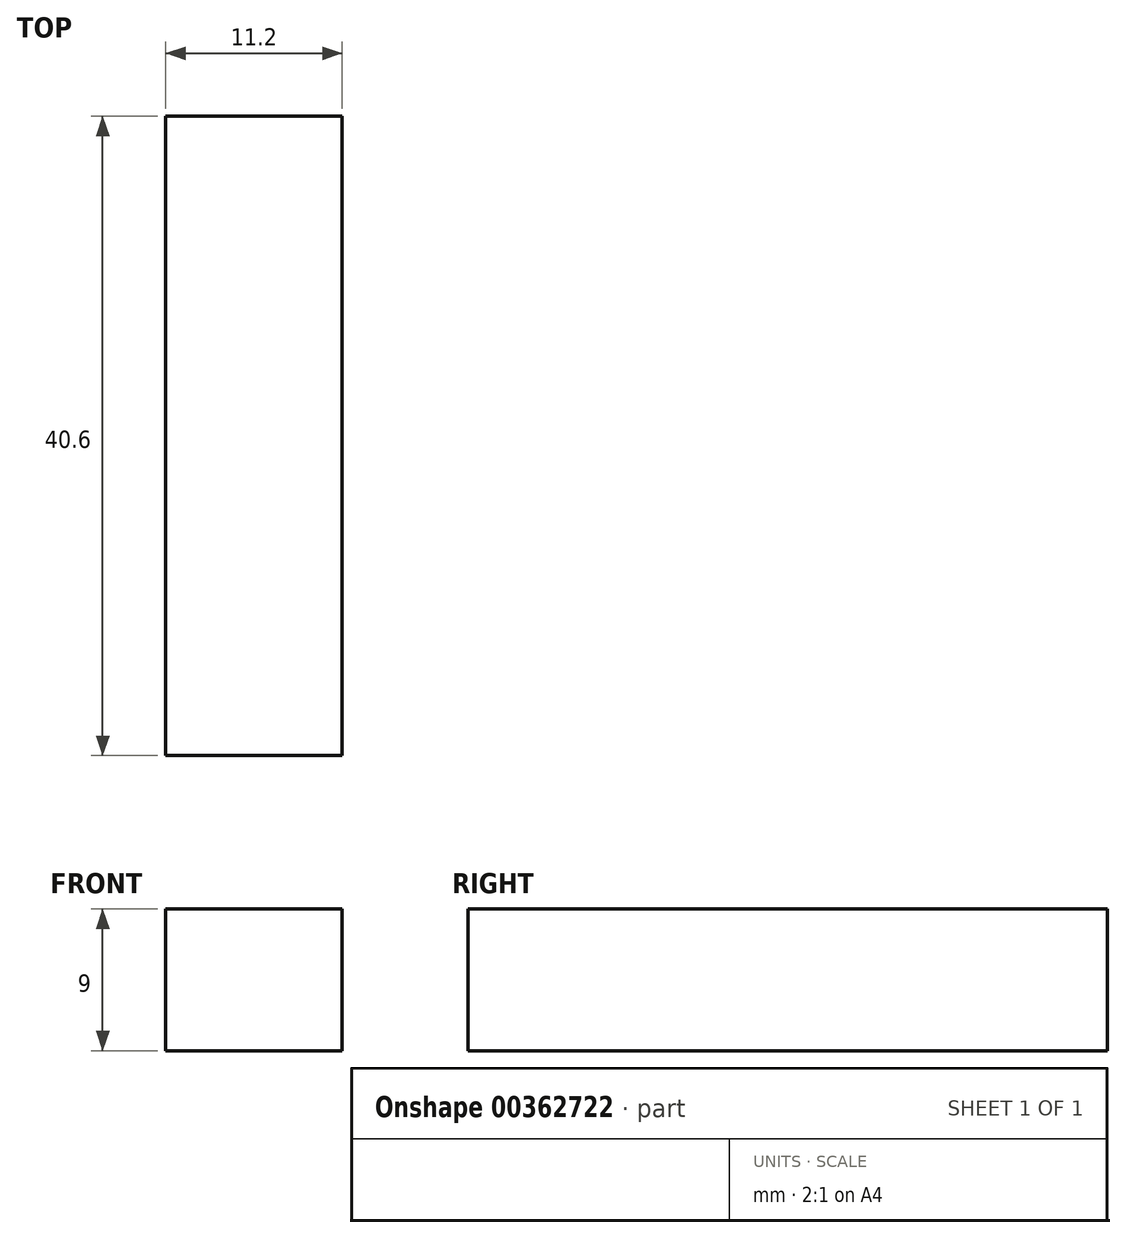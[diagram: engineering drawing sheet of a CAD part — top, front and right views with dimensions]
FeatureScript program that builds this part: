
annotation { "Feature Type Name" : "Feature", "Feature Type Description" : "" }
export const myFeature = defineFeature(function(context is Context, id is Id, definition is map)
    precondition{}
    {
        {
            var Q0;
            Q0=qCreatedBy(makeId("Front.planeOp"),FACE);
            var sketch = newSketch(context, id + "F0", { "sketchPlane" : qUnion([Q0])});
            skLineSegment(sketch, "E0.bottom", {"start": v(5.6, -4.5) * mm, "end": v(-5.6, -4.5) * mm});
            skLineSegment(sketch, "E0.top", {"start": v(5.6, 4.5) * mm, "end": v(-5.6, 4.5) * mm});
            skLineSegment(sketch, "E0.left", {"start": v(5.6, -4.5) * mm, "end": v(5.6, 4.5) * mm});
            skLineSegment(sketch, "E0.right", {"start": v(-5.6, -4.5) * mm, "end": v(-5.6, 4.5) * mm});
            skPoint(sketch, "E0.middle", {"position": v(0, 0) * mm});
            skSolve(sketch);
        }
        {
            var Q0;
            Q0=makeQuery(id+"F0.imprint","IMPRINT",FACE,{"disambiguationData":[TD([[makeQuery(id+"F0.imprint","IMPRINT",EDGE,{"derivedFrom":sQuery(id+"F0.wireOp",EDGE,"E0.bottom")}),-1.0]])]});
            extrude(context, id + "F1", {"entities" : qUnion([Q0]), "depth" : 40.6 * mm});
        }
    });
